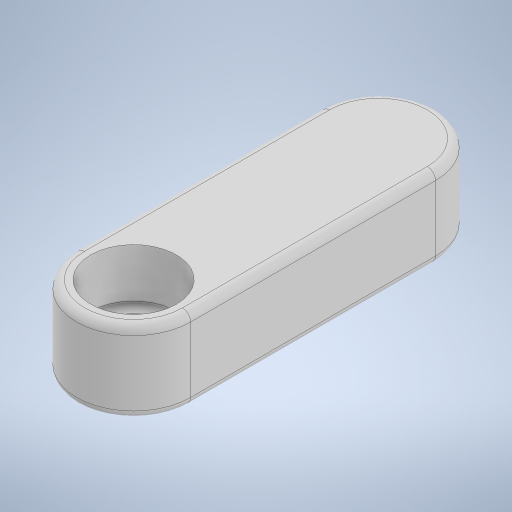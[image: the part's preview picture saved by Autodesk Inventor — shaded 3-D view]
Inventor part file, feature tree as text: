
AUTODESK INVENTOR PART (.ipt)
format: ipt  version: 2024.2 (Build 282272000, 272)  size: 273,920 bytes
history: native  units: mm
features: extrude x2, sketch x2, fillet x1
ambient origin geometry x8: Origin, YZ Plane, XZ Plane, XY Plane, X Axis, Y Axis, Z Axis, Center Point
bodies: Solid1 (feature_tree)
feature tree (5):
  extrude  "Extrusion1"  Depth=15.0mm
  extrude  "Extrusion2"  Depth=5.0mm TaperAngle=0.0deg
  fillet  "Fillet1"  Radius=5.25mm
  sketch  "Sketch1"  dims[d0=7.0mm d1=15.0mm]
  sketch  "Sketch2"  dims[d2=3.4mm d3=5.0mm d4=0.0mm d5=5.25mm d6=3.0mm d7=0.0mm d8=0.5mm]
